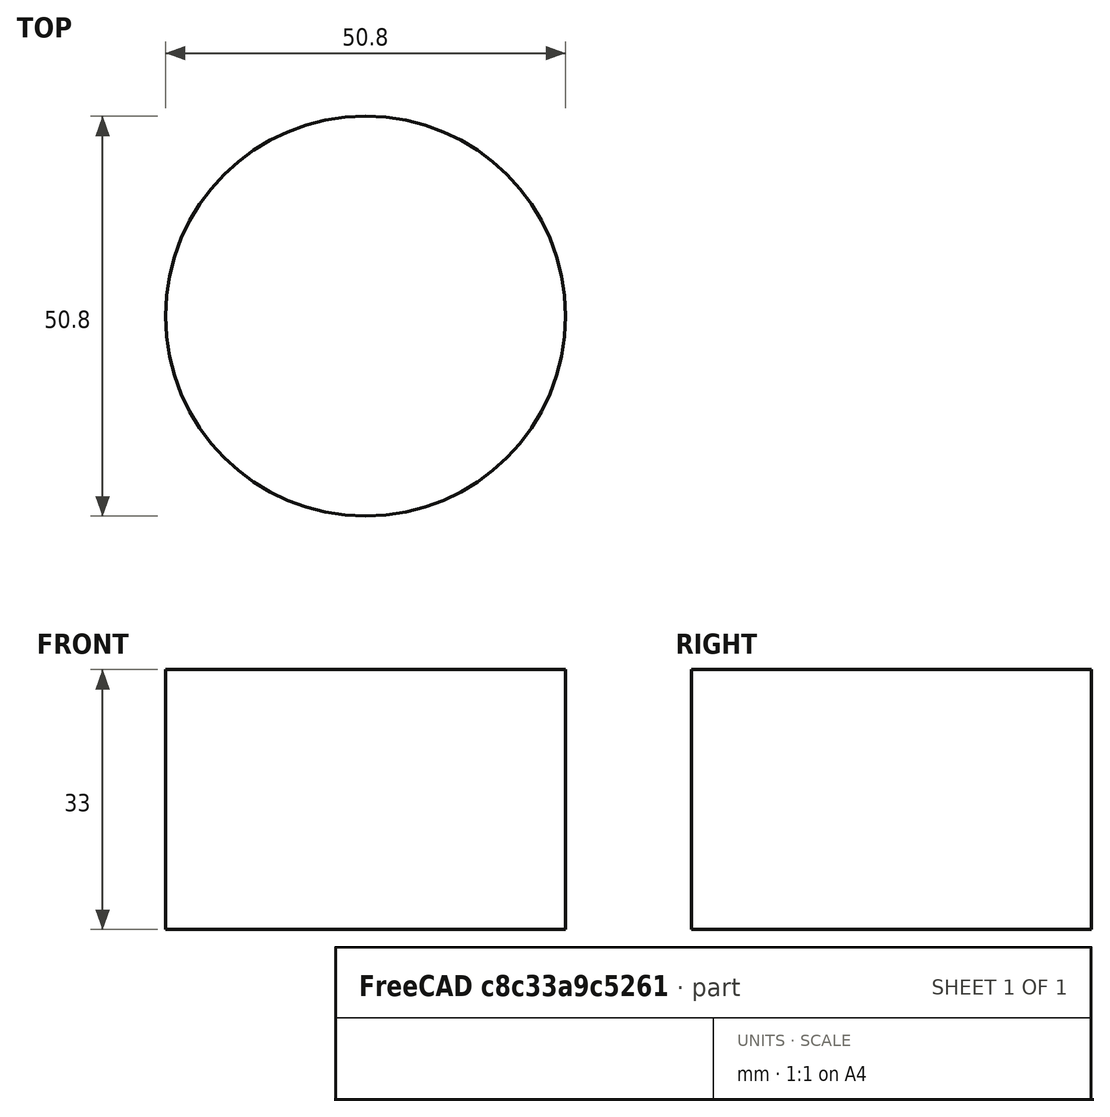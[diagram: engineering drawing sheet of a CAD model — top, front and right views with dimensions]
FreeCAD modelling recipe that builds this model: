
FCSTD DOCUMENT  (FreeCAD 0.17R13509 (Git))
Label: FTInsulator1
License: All rights reserved
LicenseURL: http://en.wikipedia.org/wiki/All_rights_reserved
objects: Part::Cylinder×5, Path::FeaturePython×5, Part::MultiFuse×2, Part::FeaturePython×2, Part::Box×1, Part::Cut×1, App::FeaturePython×1, Path::FeatureCompoundPython×1
note: 14 computed .brp shape members not serialized (recipe doc carries the construction recipe); baked Part::Feature solids carry a one-line shape summary decoded from their .brp

FEATURE [Part::Cylinder] Cylinder084  label="Feedthrough005"
  Angle = 360
  AttacherType = Attacher::AttachEngine3D
  Height = 5
  Placement = pos=(73.66,148,-10) rot=(0,0,1;0rad)
  Radius = 17
  expr: Radius = 17
  expr: Placement.Base.x = 210.81999999999999 / 2 - 31.75
FEATURE [Part::Cylinder] Cylinder088  label="Feedthrough008"
  Angle = 360
  AttacherType = Attacher::AttachEngine3D
  Height = 33
  Placement = pos=(73.66,148,-10) rot=(0,0,1;0rad)
  Radius = 14
  expr: Radius = 28 / 2
  expr: Placement.Base.x = 210.81999999999999 / 2 - 31.75
FEATURE [Part::Cylinder] Cylinder090  label="FTInsInnerHole"
  Angle = 360
  AttacherType = Attacher::AttachEngine3D
  Height = 33
  Placement = pos=(73.66,148,-10) rot=(0,0,1;0rad)
  Radius = 11.7
  expr: Placement.Base.x = 210.81999999999999 / 2 - 31.75
FEATURE [Part::Box] Box016  label="FTInsLug"
  AttacherType = Attacher::AttachEngine3D
  Height = 1
  Length = 1
  Placement = pos=(63,136,-8) rot=(0,0,1;0rad)
  Width = 1
FEATURE [Part::Cylinder] Cylinder093  label="FTInsMount1"
  Angle = 360
  AttacherType = Attacher::AttachEngine3D
  Height = 14
  Placement = pos=(53.66,148,-15) rot=(0,0,1;0rad)
  Radius = 1.5
  expr: Placement.Base.x = 73.659999999999997 - 20
FEATURE [Part::Cylinder] Cylinder094  label="FTInsMount2"
  Angle = 360
  AttacherType = Attacher::AttachEngine3D
  Height = 14
  Placement = pos=(93.66,148,-14) rot=(0,0,1;0rad)
  Radius = 1.5
  expr: Placement.Base.x = 73.659999999999997 + 20
FEATURE [Part::MultiFuse] Fusion038
  Shapes = -> [Cylinder084,Cylinder088,Box016]
FEATURE [Part::MultiFuse] Fusion039
  Shapes = -> [Cylinder094,Cylinder093,Cylinder090]
FEATURE [Part::Cut] Cut010  label="FTInsulator1"
  Base = -> Fusion038
  Placement = pos=(-73.66,-148,-23) rot=(0,0,1;0rad)
  Tool = -> Fusion039
  expr: Placement.Base.z = -33 + 10
FEATURE [App::FeaturePython] SetupSheet  # Path/CAM operation (typed FeaturePython)
  ClearanceHeightExpression = StartDepth+SetupSheet.ClearanceHeightOffset
  ClearanceHeightOffset = 5
  FinalDepthExpression = OpFinalDepth
  HorizRapid = 0
  SafeHeightExpression = StartDepth+SetupSheet.SafeHeightOffset
  SafeHeightOffset = 3
  StartDepthExpression = OpStartDepth
  StepDownExpression = OpToolDiameter
  VertRapid = 0
FEATURE [Part::FeaturePython] Clone  label="Base-FTInsulator1"  # Draft clone (typed FeaturePython)
  AttacherType = Attacher::AttachEngine3D
  Fuse = false
  Objects = -> [Cut010]
  PathResource = Base
  Placement = pos=(-73.66,-148,-23) rot=(0,0,1;0rad)
  Scale = (1,1,1)
FEATURE [Part::FeaturePython] Stock001  # WARN: FeaturePython — macro-defined, semantics opaque (R4)
  Height = 33
  Placement = pos=(0,0,-33) rot=(0,0,1;0rad)
  Radius = 25.4
  StockType = CreateCylinder
FEATURE [Path::FeaturePython] T2__250_End_Mill  label="T2: 250 End Mill"  # Path/CAM operation (typed FeaturePython)
  HorizFeed = 1500
  HorizRapid = 0
  SpindleDir = 0
  SpindleSpeed = 24000
  ToolNumber = 2
  VertFeed = 35
  VertRapid = 0
  expr: HorizRapid = SetupSheet.HorizRapid
  expr: VertRapid = SetupSheet.VertRapid
FEATURE [Path::FeaturePython] Profile_Faces  # Path/CAM operation (typed FeaturePython)
  Active = true
  AreaParams:
    OpenMode = 0
    Angle = 45.0
    MinArcPoints = 4
    Coplanar = 0
    Tolerance = 1e-07
    CleanDistance = 0.0
    PocketExtraOffset = 0.0
    RoundPrecision = 0.0
    AngleShift = 0.0
    SubjectFill = 0
    PocketMode = 0
    Simplify = False
    SectionTolerance = 1e-06
    MaxArcPoints = 100
    Offset = 3.175
    Accuracy = 0.01
    PocketStepover = 0.0
    ClipFill = 0
    ToolRadius = 1.0
    Outline = False
    ClipperScale = 10000000.0
    FromCenter = False
    Explode = False
    EndType = 0
    Shift = 0.0
    ExtraPass = 0
    Project = False
    JoinType = 0
    Thicken = False
    Stepdown = 1.0
    SectionMode = 2
    MiterLimit = 2.0
    Deflection = 0.01
    Reorient = True
    FitArcs = True
    SectionCount = -1
    SectionOffset = 0.0
    Stepover = 0.0
    Unit = 1.0
    Fill = 0
  Base = -> [Clone]
  ClearanceHeight = 5
  Direction = 0
  FinalDepth = -28
  JoinType = 0
  MiterLimit = 0.1
  OffsetExtra = 0
  OpFinalDepth = -28
  OpStartDepth = 0
  OpToolDiameter = 6.35
  PathParams = {'resume_height': 3.0, 'feedrate': 1500.0, 'verbose': True, 'orientation': 1, 'return_end': True, 'preamble': False, 'retraction': 5.0, 'feedrate_v': 35.0}
  SafeHeight = 3
  Side = 0
  StartDepth = 0
  StartPoint = (0,0,0)
  StepDown = 1.5
  ToolController = -> T2__250_End_Mill
  UseComp = true
  UseStartPoint = false
  processCircles = false
  processHoles = false
  processPerimeter = true
  expr: ClearanceHeight = StartDepth + SetupSheet.ClearanceHeightOffset
  expr: SafeHeight = StartDepth + SetupSheet.SafeHeightOffset
  expr: StepDown = 1.5
  expr: FinalDepth = OpFinalDepth
  expr: StartDepth = OpStartDepth
FEATURE [Path::FeaturePython] Profile_Faces001  # Path/CAM operation (typed FeaturePython)
  Active = true
  AreaParams:
    OpenMode = 0
    Angle = 45.0
    MinArcPoints = 4
    Coplanar = 0
    Tolerance = 1e-07
    CleanDistance = 0.0
    PocketExtraOffset = 0.0
    RoundPrecision = 0.0
    AngleShift = 0.0
    SubjectFill = 0
    PocketMode = 0
    Simplify = False
    SectionTolerance = 1e-06
    MaxArcPoints = 100
    Offset = 3.175
    Accuracy = 0.01
    PocketStepover = 0.0
    ClipFill = 0
    ToolRadius = 1.0
    Outline = False
    ClipperScale = 10000000.0
    FromCenter = False
    Explode = False
    EndType = 0
    Shift = 0.0
    ExtraPass = 0
    Project = False
    JoinType = 0
    Thicken = False
    Stepdown = 1.0
    SectionMode = 2
    MiterLimit = 2.0
    Deflection = 0.01
    Reorient = True
    FitArcs = True
    SectionCount = -1
    SectionOffset = 0.0
    Stepover = 0.0
    Unit = 1.0
    Fill = 0
  Base = -> [Clone]
  ClearanceHeight = 5
  Direction = 0
  FinalDepth = -33
  JoinType = 0
  MiterLimit = 0.1
  OffsetExtra = 0
  OpFinalDepth = -33
  OpStartDepth = 0
  OpToolDiameter = 6.35
  PathParams = {'resume_height': 3.0, 'feedrate': 1500.0, 'verbose': True, 'orientation': 1, 'return_end': True, 'preamble': False, 'retraction': 5.0, 'feedrate_v': 35.0}
  SafeHeight = 3
  Side = 0
  StartDepth = 0
  StartPoint = (0,0,0)
  StepDown = 1.5
  ToolController = -> T2__250_End_Mill
  UseComp = true
  UseStartPoint = false
  processCircles = false
  processHoles = false
  processPerimeter = true
  expr: ClearanceHeight = StartDepth + SetupSheet.ClearanceHeightOffset
  expr: SafeHeight = StartDepth + SetupSheet.SafeHeightOffset
  expr: StepDown = 1.5
  expr: FinalDepth = OpFinalDepth
  expr: StartDepth = OpStartDepth
FEATURE [Path::FeaturePython] Pocket_Shape  # Path/CAM operation (typed FeaturePython)
  Active = true
  AreaParams:
    OpenMode = 0
    Angle = 45.0
    MinArcPoints = 4
    Coplanar = 0
    Tolerance = 1e-07
    CleanDistance = 0.0
    PocketExtraOffset = 0.0
    RoundPrecision = 0.0
    AngleShift = 0.0
    SubjectFill = 0
    PocketMode = 3
    Simplify = False
    SectionTolerance = 1e-06
    MaxArcPoints = 100
    Offset = 0.0
    Accuracy = 0.01
    PocketStepover = 3.175
    ClipFill = 0
    ToolRadius = 3.175
    Outline = False
    ClipperScale = 10000000.0
    FromCenter = True
    Explode = False
    EndType = 0
    Shift = 0.0
    ExtraPass = 0
    Project = False
    JoinType = 0
    Thicken = False
    Stepdown = 1.0
    SectionMode = 2
    MiterLimit = 2.0
    Deflection = 0.01
    Reorient = True
    FitArcs = True
    SectionCount = -1
    SectionOffset = 0.0
    Stepover = 0.0
    Unit = 1.0
    Fill = 0
  Base = -> [Clone]
  ClearanceHeight = 5
  CutMode = 0
  ExtraOffset = 0
  FinalDepth = -33
  FinishDepth = 0
  KeepToolDown = false
  MinTravel = false
  OffsetPattern = 2
  OpFinalDepth = -33
  OpStartDepth = 0
  OpToolDiameter = 6.35
  PathParams = {'resume_height': 3.0, 'feedrate': 1500.0, 'verbose': True, 'orientation': 1, 'return_end': True, 'preamble': False, 'retraction': 5.0, 'feedrate_v': 35.0}
  SafeHeight = 3
  StartAt = 0
  StartDepth = 0
  StartPoint = (0,0,0)
  StepDown = 1.5
  StepOver = 50
  ToolController = -> T2__250_End_Mill
  UseStartPoint = false
  ZigZagAngle = 45
  expr: ClearanceHeight = StartDepth + SetupSheet.ClearanceHeightOffset
  expr: SafeHeight = StartDepth + SetupSheet.SafeHeightOffset
  expr: StepDown = 1.5
  expr: FinalDepth = OpFinalDepth
  expr: StartDepth = OpStartDepth
FEATURE [Path::FeatureCompoundPython] Operations  # Path/CAM operation (typed FeaturePython)
  Group = -> [Profile_Faces,Profile_Faces001,Pocket_Shape]
  UsePlacements = false
FEATURE [Path::FeaturePython] Job  # Path/CAM operation (typed FeaturePython)
  Base = -> Clone
  GeometryTolerance = 0.01
  Operations = -> Operations
  PostProcessor = 5
  PostProcessorOutputFile = <userpath>/Documents/CNC/chamber_plate/fts/ftinsulator1_new_250_roughing.ngc
  SetupSheet = -> SetupSheet
  Stock = -> Stock001
  ToolController = -> [T2__250_End_Mill]
